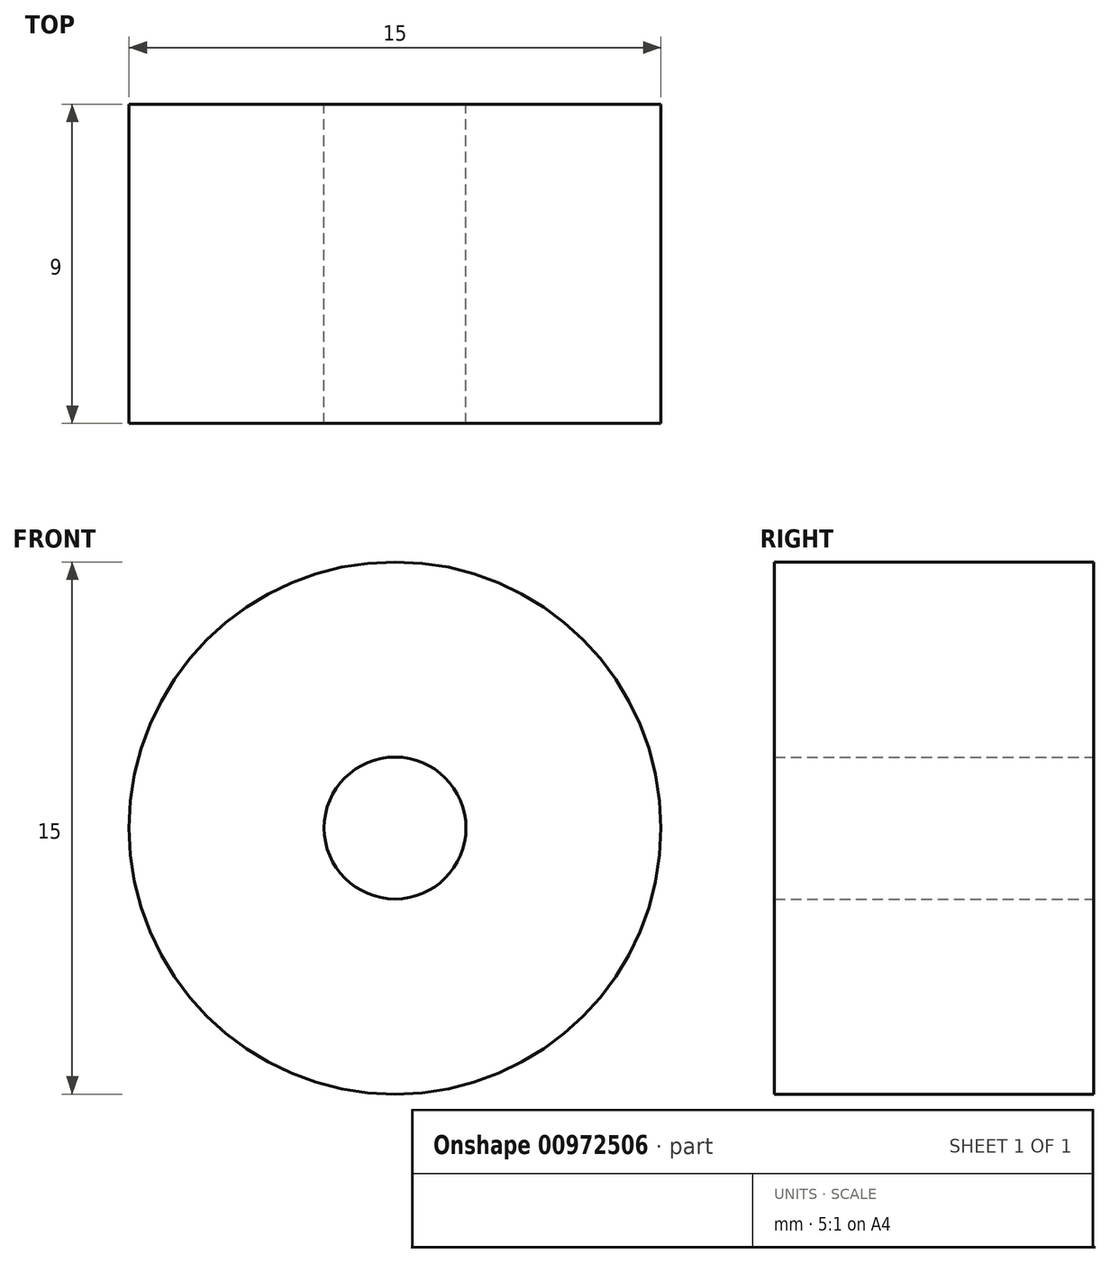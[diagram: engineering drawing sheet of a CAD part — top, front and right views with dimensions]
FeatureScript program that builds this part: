
annotation { "Feature Type Name" : "Feature", "Feature Type Description" : "" }
export const myFeature = defineFeature(function(context is Context, id is Id, definition is map)
    precondition{}
    {
        {
            var Q0;
            Q0=qCreatedBy(makeId("Front.planeOp"),FACE);
            var sketch = newSketch(context, id + "F0", { "sketchPlane" : qUnion([Q0])});
            skCircle(sketch, "E0", {"center": v(0, 0) * mm, "radius": 2 * mm});
            skCircle(sketch, "E1", {"center": v(0, 0) * mm, "radius": 7.5 * mm});
            skSolve(sketch);
        }
        {
            var Q0;
            Q0=makeQuery(id+"F0.imprint","IMPRINT",FACE,{"disambiguationData":[TD([[makeQuery(id+"F0.imprint","IMPRINT",EDGE,{"derivedFrom":sQuery(id+"F0.wireOp",EDGE,"E0")}),-1.0]])]});
            extrude(context, id + "F1", {"entities" : qUnion([Q0]), "endBound" : BoundingType.SYMMETRIC, "depth" : 9 * mm, "offsetDistance" : 25 * mm});
        }
    });
